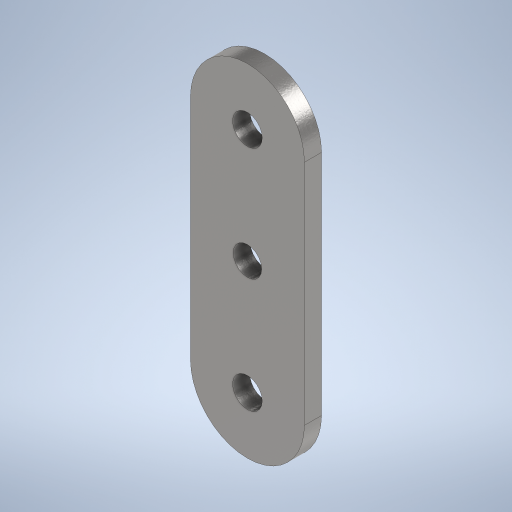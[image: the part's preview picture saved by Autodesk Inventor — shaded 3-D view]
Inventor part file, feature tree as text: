
AUTODESK INVENTOR PART (.ipt)
format: ipt  version: 2024.2 (Build 282272000, 272)  size: 243,200 bytes
history: native  units: mm
features: extrude x1, sketch x1
ambient origin geometry x8: Origin, YZ Plane, XZ Plane, XY Plane, X Axis, Y Axis, Z Axis, Center Point
bodies: Solid1 (feature_tree)
feature tree (2):
  extrude  "Extrusion1"  Depth=20.0mm
  sketch  "Sketch1"  dims[d8=3.0mm d9=0.0mm d15=20.0mm d16=20.0mm d17=40.0mm d18=10.0mm d19=5.2mm d20=5.0mm]
